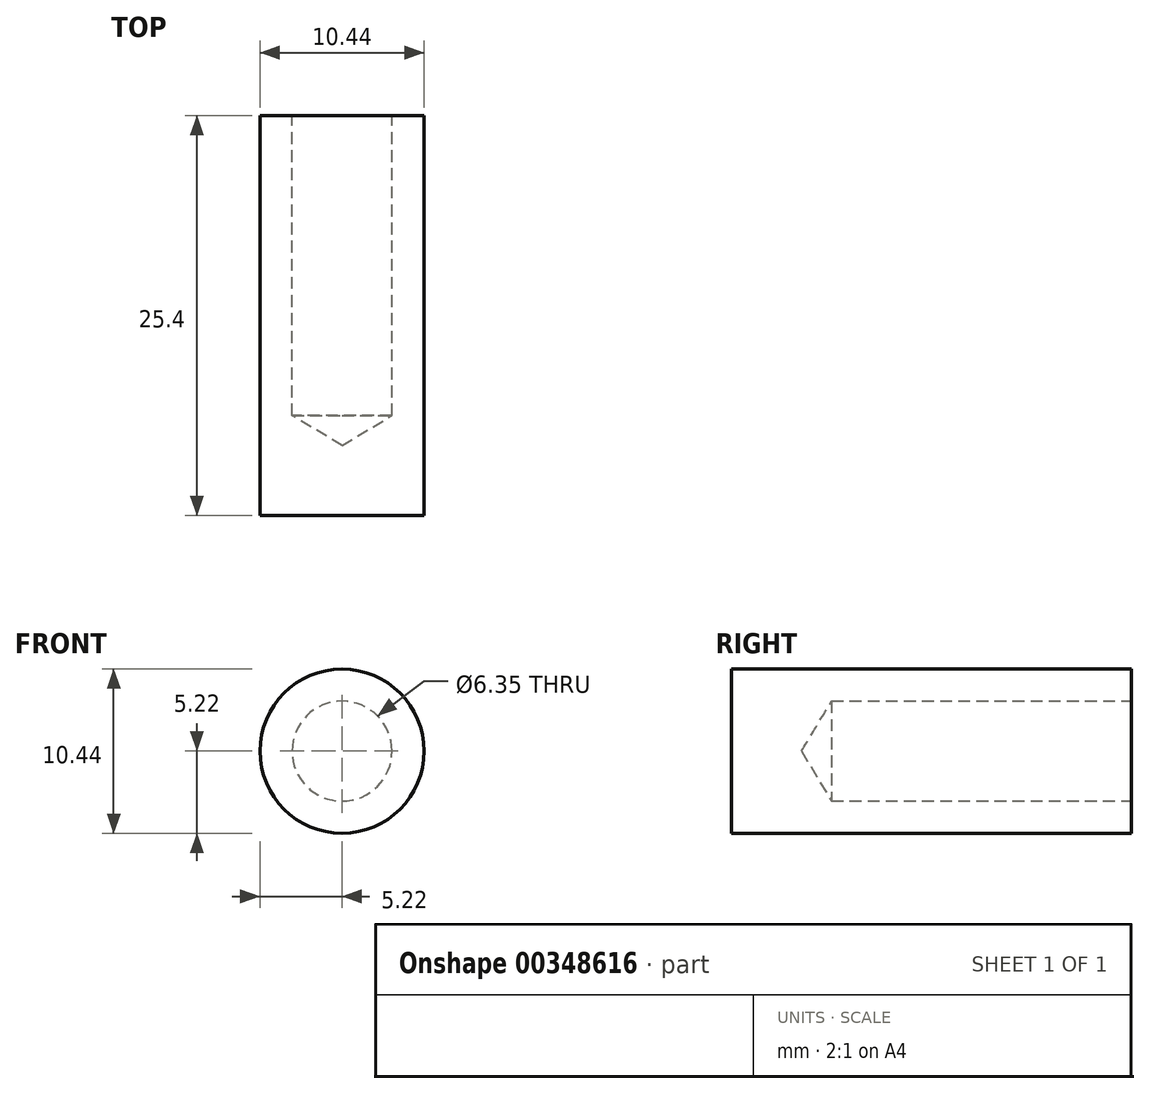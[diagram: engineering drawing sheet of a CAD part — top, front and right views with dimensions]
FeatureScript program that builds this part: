
annotation { "Feature Type Name" : "Feature", "Feature Type Description" : "" }
export const myFeature = defineFeature(function(context is Context, id is Id, definition is map)
    precondition{}
    {
        {
            var Q0;
            Q0=qCreatedBy(makeId("Front.planeOp"),FACE);
            var sketch = newSketch(context, id + "F0", { "sketchPlane" : qUnion([Q0])});
            skCircle(sketch, "E0", {"center": v(0, 0) * mm, "radius": 5.22 * mm});
            skSolve(sketch);
        }
        {
            var Q0;
            Q0=makeQuery(id+"F0.imprint","IMPRINT",FACE,{"disambiguationData":[TD([[makeQuery(id+"F0.imprint","IMPRINT",EDGE,{"derivedFrom":sQuery(id+"F0.wireOp",EDGE,"E0")}),1.0]])]});
            extrude(context, id + "F1", {"entities" : qUnion([Q0]), "depth" : 25.4 * mm});
        }
        {
            var Q0;
            Q0=sQuery(id+"F0.wireOp",VERTEX,"E0.center");
            var Q1;
            Q1=makeQuery(id+"F1.opExtrude","SWEPT_BODY",BODY,{"disambiguationData":[OSD([sQuery(id+"F0.wireOp",EDGE,"E0")])]});
            hole(context, id + "F2", {"style" : HoleStyle.SIMPLE, "endStyle" : HoleEndStyle.BLIND, "oppositeDirection" : true, "holeDiameter" : 6.35 * mm, "holeDepth" : 19.05 * mm, "isTappedThrough" : true, "tappedDepth" : 12.7 * mm, "tapClearance" : 3, "startFromSketch" : true, "locations" : qUnion([Q0]), "scope" : qUnion([Q1])});
        }
    });
